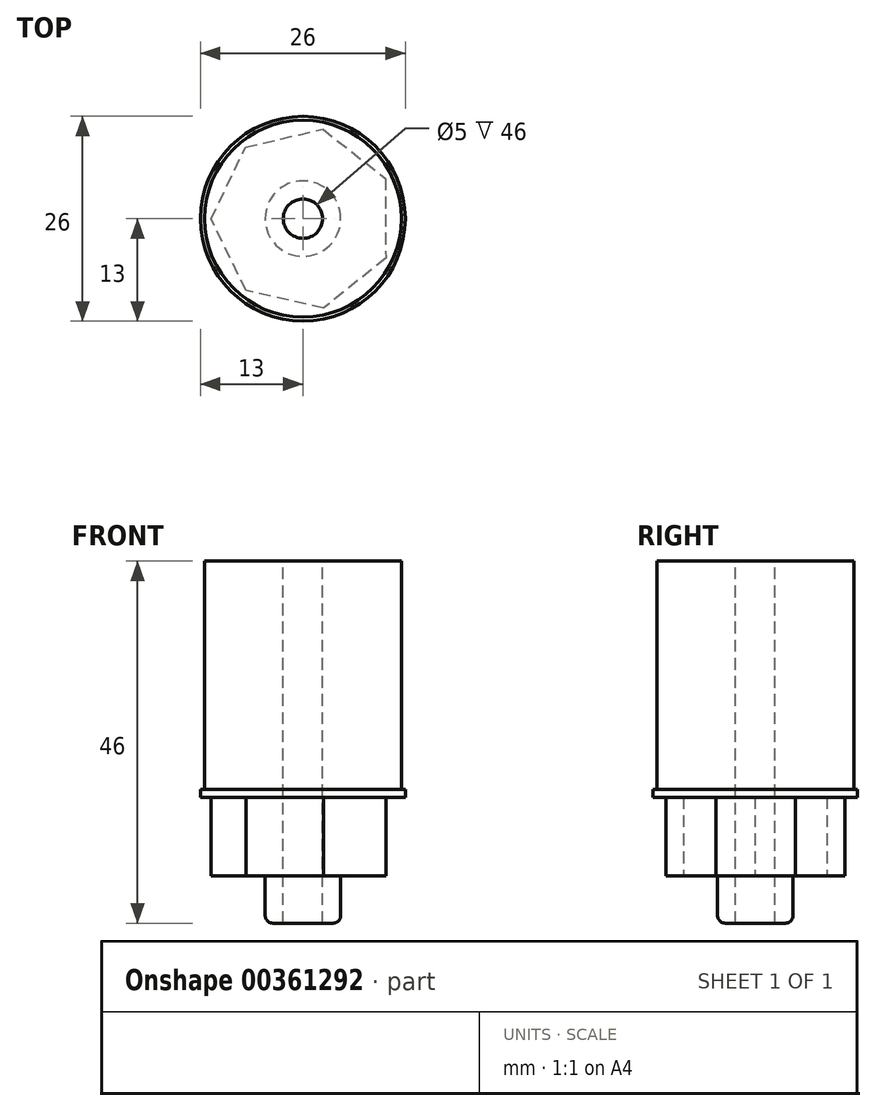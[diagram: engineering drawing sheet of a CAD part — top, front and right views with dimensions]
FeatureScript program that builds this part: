
annotation { "Feature Type Name" : "Feature", "Feature Type Description" : "" }
export const myFeature = defineFeature(function(context is Context, id is Id, definition is map)
    precondition{}
    {
        {
            var Q0;
            Q0=qCreatedBy(makeId("Top.planeOp"),FACE);
            var sketch = newSketch(context, id + "F0", { "sketchPlane" : qUnion([Q0])});
            skCircle(sketch, "E0.cCircle", {"center": v(0, 0) * mm, "radius": 10.5 * mm, "construction": true});
            skLineSegment(sketch, "E0.0", {"start": v(10.52, -5.01) * mm, "end": v(2.64, -11.35) * mm});
            skLineSegment(sketch, "E0.1", {"start": v(2.64, -11.35) * mm, "end": v(-7.23, -9.14) * mm});
            skLineSegment(sketch, "E0.2", {"start": v(-7.23, -9.14) * mm, "end": v(-11.65, -0.05) * mm});
            skLineSegment(sketch, "E0.3", {"start": v(-11.65, -0.05) * mm, "end": v(-7.3, 9.08) * mm});
            skLineSegment(sketch, "E0.4", {"start": v(-7.3, 9.08) * mm, "end": v(2.55, 11.37) * mm});
            skLineSegment(sketch, "E0.5", {"start": v(2.55, 11.37) * mm, "end": v(10.48, 5.1) * mm});
            skLineSegment(sketch, "E0.6", {"start": v(10.48, 5.1) * mm, "end": v(10.52, -5.01) * mm});
            skPoint(sketch, "E0.0.midPoint", {"position": v(6.58, -8.18) * mm});
            skCircle(sketch, "E1", {"center": v(0, 0) * mm, "radius": 4.8 * mm});
            skCircle(sketch, "E2", {"center": v(0, 0) * mm, "radius": 12.5 * mm});
            skCircle(sketch, "E3", {"center": v(0, 0) * mm, "radius": 2.5 * mm});
            skCircle(sketch, "E4", {"center": v(0, 0) * mm, "radius": 13 * mm});
            skSolve(sketch);
        }
        {
            var Q0;
            Q0=makeQuery(id+"F0.imprint","IMPRINT",FACE,{"disambiguationData":[TD([[makeQuery(id+"F0.imprint","IMPRINT",EDGE,{"derivedFrom":sQuery(id+"F0.wireOp",EDGE,"E1")}),1.0]])]});
            extrude(context, id + "F1", {"entities" : qUnion([Q0]), "oppositeDirection" : true, "depth" : 6 * mm});
        }
        {
            var Q0;
            Q0=makeQuery(id+"F0.imprint","IMPRINT",FACE,{"disambiguationData":[TD([[makeQuery(id+"F0.imprint","IMPRINT",EDGE,{"derivedFrom":sQuery(id+"F0.wireOp",EDGE,"E0.0")}),-1.0]])]});
            var Q1;
            Q1=makeQuery(id+"F0.imprint","IMPRINT",FACE,{"disambiguationData":[TD([[makeQuery(id+"F0.imprint","IMPRINT",EDGE,{"derivedFrom":sQuery(id+"F0.wireOp",EDGE,"E1")}),1.0]])]});
            extrude(context, id + "F2", {"entities" : qUnion([Q0, Q1]), "operationType" : NewBodyOperationType.ADD, "depth" : 40 * mm});
        }
        {
            var Q0;
            Q0=makeQuery(id+"F0.imprint","IMPRINT",FACE,{"disambiguationData":[TD([[makeQuery(id+"F0.imprint","IMPRINT",EDGE,{"derivedFrom":sQuery(id+"F0.wireOp",EDGE,"E0.0")}),1.0]])]});
            extrude(context, id + "F3", {"entities" : qUnion([Q0]), "operationType" : NewBodyOperationType.ADD, "depth" : 40 * mm});
        }
        {
            var Q0;
            Q0=makeQuery(id+"F0.imprint","IMPRINT",FACE,{"disambiguationData":[TD([[makeQuery(id+"F0.imprint","IMPRINT",EDGE,{"derivedFrom":sQuery(id+"F0.wireOp",EDGE,"E0.0")}),1.0]])]});
            extrude(context, id + "F4", {"entities" : qUnion([Q0]), "operationType" : NewBodyOperationType.REMOVE, "depth" : 10 * mm});
        }
        {
            var Q0;
            Q0=makeQuery(id+"F0.imprint","IMPRINT",FACE,{"disambiguationData":[TD([[makeQuery(id+"F0.imprint","IMPRINT",EDGE,{"derivedFrom":sQuery(id+"F0.wireOp",EDGE,"E2")}),-1.0]])]});
            extrude(context, id + "F5", {"entities" : qUnion([Q0]), "operationType" : NewBodyOperationType.ADD, "depth" : 11 * mm});
        }
        {
            var Q0;
            Q0=makeQuery(id+"F0.imprint","IMPRINT",FACE,{"disambiguationData":[TD([[makeQuery(id+"F0.imprint","IMPRINT",EDGE,{"derivedFrom":sQuery(id+"F0.wireOp",EDGE,"E2")}),-1.0]])]});
            extrude(context, id + "F6", {"entities" : qUnion([Q0]), "operationType" : NewBodyOperationType.REMOVE, "depth" : 10 * mm});
        }
        {
            var Q0;
            Q0=makeQuery(id+"F1.opExtrude","CAP_EDGE",EDGE,{"disambiguationData":[OSD([sQuery(id+"F0.wireOp",EDGE,"E1")])],"isStart":false});
            fillet(context, id + "F7", {"entities" : qUnion([Q0]), "radius" : 1 * mm, "tangentPropagation" : true, "allowEdgeOverflow" : false});
        }
    });
